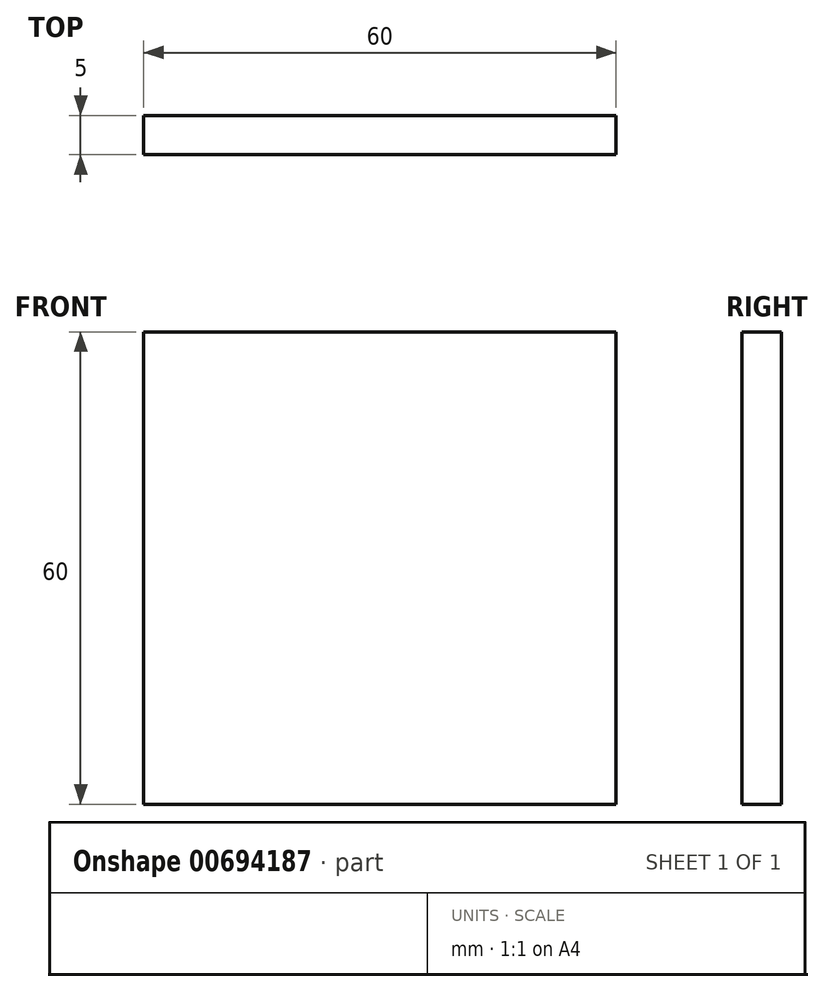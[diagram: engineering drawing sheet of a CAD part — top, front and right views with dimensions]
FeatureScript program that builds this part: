
annotation { "Feature Type Name" : "Feature", "Feature Type Description" : "" }
export const myFeature = defineFeature(function(context is Context, id is Id, definition is map)
    precondition{}
    {
        {
            var Q0;
            Q0=qCreatedBy(makeId("Front.planeOp"),FACE);
            var sketch = newSketch(context, id + "F0", { "sketchPlane" : qUnion([Q0])});
            skLineSegment(sketch, "E0.bottom", {"start": v(-23.13, 42.98) * mm, "end": v(36.87, 42.98) * mm});
            skLineSegment(sketch, "E0.top", {"start": v(-23.13, -17.02) * mm, "end": v(36.87, -17.02) * mm});
            skLineSegment(sketch, "E0.left", {"start": v(-23.13, 42.98) * mm, "end": v(-23.13, -17.02) * mm});
            skLineSegment(sketch, "E0.right", {"start": v(36.87, 42.98) * mm, "end": v(36.87, -17.02) * mm});
            skSolve(sketch);
        }
        {
            var Q0;
            Q0=makeQuery(id+"F0.imprint","IMPRINT",FACE,{"disambiguationData":[TD([[makeQuery(id+"F0.imprint","IMPRINT",EDGE,{"derivedFrom":sQuery(id+"F0.wireOp",EDGE,"E0.bottom")}),-1.0]])]});
            extrude(context, id + "F1", {"entities" : qUnion([Q0]), "depth" : 5 * mm, "offsetDistance" : 25 * mm});
        }
    });
